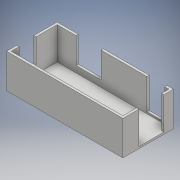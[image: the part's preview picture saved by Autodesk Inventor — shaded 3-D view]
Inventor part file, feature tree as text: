
AUTODESK INVENTOR PART (.ipt)
format: ipt  version: 2018 (Build 220112000, 112)  size: 199,168 bytes
history: native  units: mm
features: extrude x9, sketch x9, chamfer x3
ambient origin geometry x8: Origin, YZ Plane, XZ Plane, XY Plane, X Axis, Y Axis, Z Axis, Center Point
bodies: Solid1 (feature_tree)
feature tree (21):
  extrude  "Extrusion1"  Depth=28.5mm
  extrude  "Extrusion2"  Depth=20.0mm TaperAngle=0.0deg
  extrude  "Extrusion3"  Depth=4.5mm
  extrude  "Extrusion4"  Depth=15.5mm
  chamfer  "Chamfer1"  Distance=1.2mm
  chamfer  "Chamfer2"  Distance=1.2mm
  extrude  "Extrusion5"  Depth=1.2mm TaperAngle=45.0deg
  chamfer  "Chamfer3"  Distance=4.0mm
  extrude  "Extrusion6"  Depth=1.2mm
  extrude  "Extrusion7"  Depth=15.5mm
  extrude  "Extrusion8"  Depth=11.7mm
  extrude  "Extrusion9"  Depth=1.2mm TaperAngle=0.0deg
  sketch  "Sketch1"  dims[d0=69.2mm d1=28.5mm]
  sketch  "Sketch2"  dims[d2=1.4mm d3=20.0mm d4=0.0mm]
  sketch  "Sketch3"  dims[d5=1.2mm d6=0.0mm d7=4.5mm]
  sketch  "Sketch4"  dims[d8=6.0mm d9=15.5mm d10=1.2mm d11=0.0mm]
  sketch  "Sketch5"  dims[d12=11.0mm]
  sketch  "Sketch6"  dims[d13=2.6mm]
  sketch  "Sketch8"  dims[d14=1.1mm]
  sketch  "Sketch9"  dims[d15=5.4mm d16=1.2mm d17=0.0mm]
  sketch  "Sketch10"  dims[d18=2.0mm d19=2.0mm d20=45.0deg d21=2.0mm d22=2.0mm d23=45.0deg d24=4.0mm d25=6.2mm d26=15.5mm d27=11.7mm d28=1.2mm d29=0.0mm d30=2.0mm d31=2.0mm d32=45.0deg d33=5.0mm d34=10.5mm d35=5.2mm d36=5.2mm d37=1.2mm d38=0.0mm d52=10.0mm d53=0.0mm d54=10.0mm d55=0.0mm d56=10.0mm d57=0.0mm]
